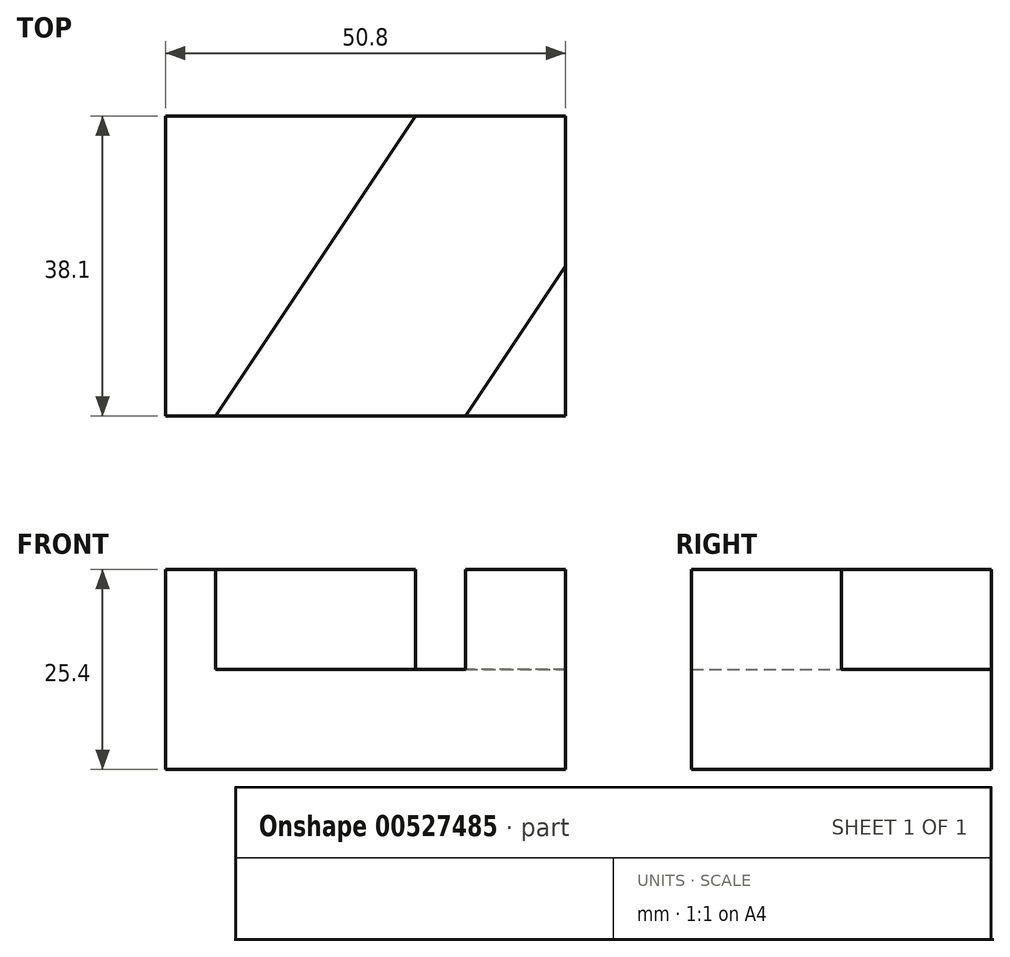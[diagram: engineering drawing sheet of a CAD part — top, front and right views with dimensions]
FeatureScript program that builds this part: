
annotation { "Feature Type Name" : "Feature", "Feature Type Description" : "" }
export const myFeature = defineFeature(function(context is Context, id is Id, definition is map)
    precondition{}
    {
        {
            var Q0;
            Q0=qCreatedBy(makeId("Front.planeOp"),FACE);
            var sketch = newSketch(context, id + "F0", { "sketchPlane" : qUnion([Q0])});
            skLineSegment(sketch, "E0", {"start": v(0, 0) * mm, "end": v(50.8, 0) * mm});
            skLineSegment(sketch, "E1", {"start": v(50.8, 0) * mm, "end": v(50.8, 25.4) * mm});
            skLineSegment(sketch, "E2", {"start": v(50.8, 25.4) * mm, "end": v(0, 25.4) * mm});
            skLineSegment(sketch, "E3", {"start": v(0, 25.4) * mm, "end": v(0, 0) * mm});
            skSolve(sketch);
        }
        {
            var Q0;
            Q0 = qSketchRegion(id + "F0", true);
            extrude(context, id + "F1", {"entities" : qUnion([Q0]), "oppositeDirection" : true, "depth" : 38.1 * mm, "offsetDistance" : 25.4 * mm});
        }
        {
            var Q0;
            Q0=makeQuery(id+"F1.opExtrude","SWEPT_FACE",FACE,{"disambiguationData":[OSD([sQuery(id+"F0.wireOp",EDGE,"E2")])]});
            var sketch = newSketch(context, id + "F2", { "sketchPlane" : qUnion([Q0])});
            skLineSegment(sketch, "E4", {"start": v(6.35, 0) * mm, "end": v(31.75, 38.1) * mm});
            skLineSegment(sketch, "E5", {"start": v(38.1, 0) * mm, "end": v(50.8, 19.05) * mm});
            skSolve(sketch);
        }
        {
            var Q0;
            {var subQ0=sQuery(id+"F2.wireOp",EDGE,"E4");Q0=makeQuery(id+"F2.imprint","IMPRINT",FACE,{"disambiguationData":[TD([[makeQuery(id+"F2.imprint","IMPRINT",EDGE,{"derivedFrom":subQ0}),-1.0]])]});}
            extrude(context, id + "F3", {"entities" : qUnion([Q0]), "operationType" : NewBodyOperationType.REMOVE, "oppositeDirection" : true, "depth" : 12.7 * mm, "offsetDistance" : 25.4 * mm});
        }
    });
